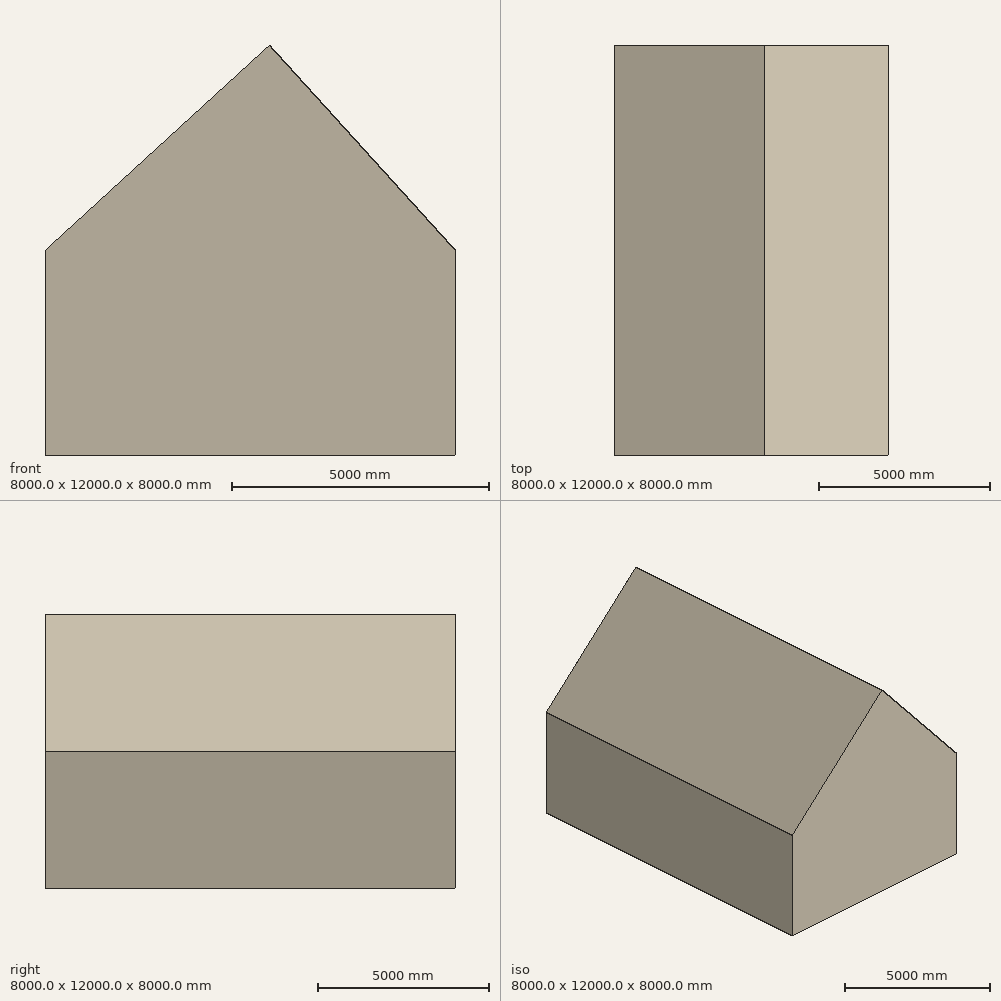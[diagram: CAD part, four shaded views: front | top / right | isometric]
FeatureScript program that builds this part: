
annotation { "Feature Type Name" : "Feature", "Feature Type Description" : "" }
export const myFeature = defineFeature(function(context is Context, id is Id, definition is map)
    precondition{}
    {
        {
            var Q0;
            Q0=qCreatedBy(makeId("Front.planeOp"),FACE);
            var sketch = newSketch(context, id + "F0", { "sketchPlane" : qUnion([Q0])});
            skLineSegment(sketch, "E0", {"start": v(0, 0) * mm, "end": v(-4374.38, 0) * mm});
            skLineSegment(sketch, "E1", {"start": v(-4374.38, 0) * mm, "end": v(-4374.38, 4000) * mm});
            skLineSegment(sketch, "E2", {"start": v(-4374.38, 4000) * mm, "end": v(3625.62, 4000) * mm});
            skLineSegment(sketch, "E3", {"start": v(3625.62, 4000) * mm, "end": v(3625.62, 0) * mm});
            skLineSegment(sketch, "E4", {"start": v(3625.62, 0) * mm, "end": v(0, 0) * mm});
            skLineSegment(sketch, "E5", {"start": v(-4374.38, 4000) * mm, "end": v(0, 8000) * mm});
            skLineSegment(sketch, "E6", {"start": v(0, 8000) * mm, "end": v(3625.62, 4000) * mm});
            skSolve(sketch);
        }
        {
            var Q0;
            Q0 = qSketchRegion(id + "F0", true);
            extrude(context, id + "F1", {"entities" : qUnion([Q0]), "depth" : 12000 * mm});
        }
    });
